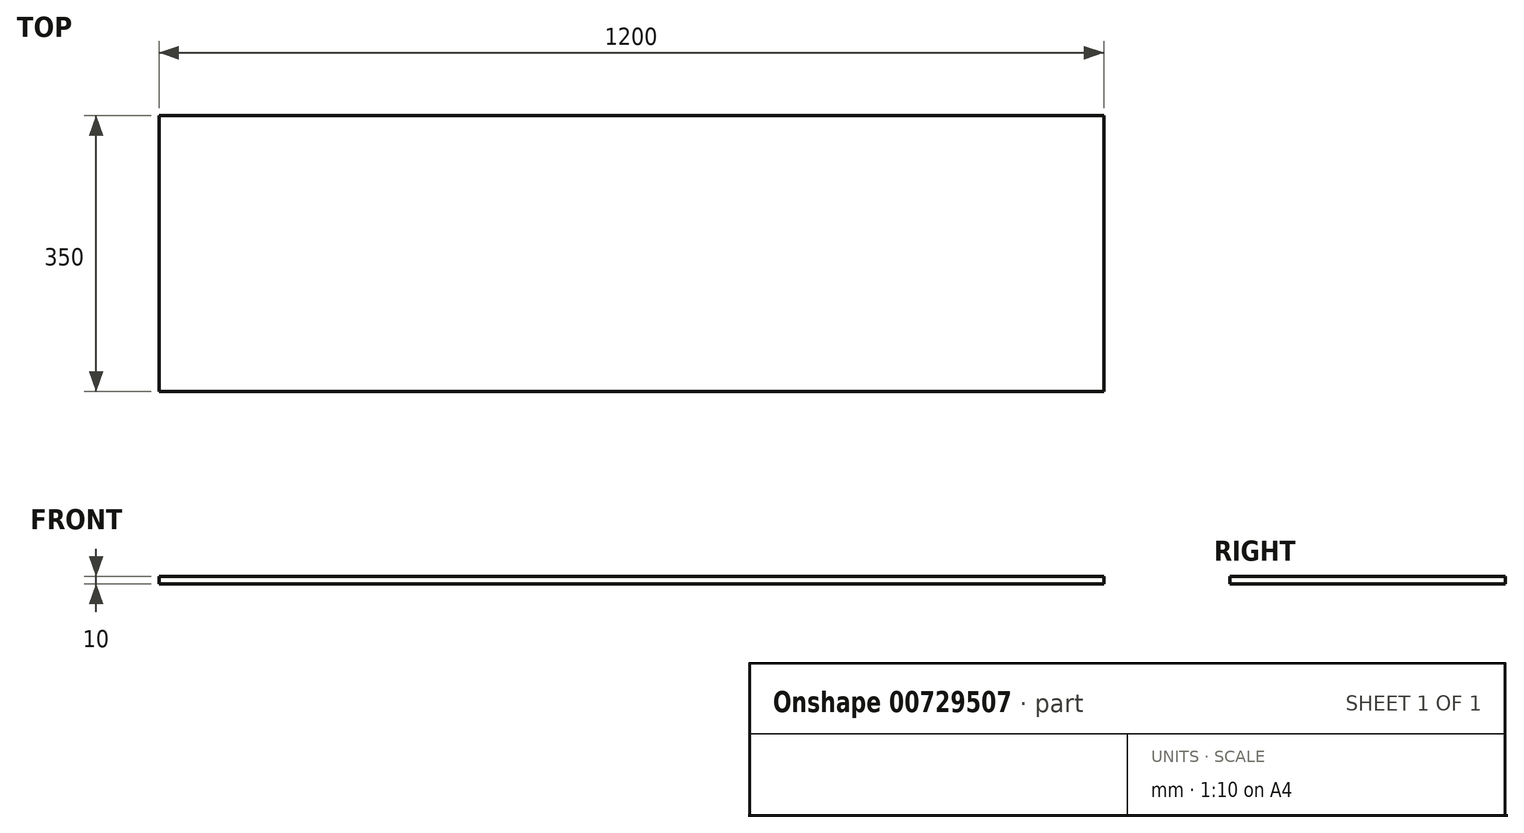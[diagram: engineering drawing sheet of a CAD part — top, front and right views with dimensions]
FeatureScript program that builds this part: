
annotation { "Feature Type Name" : "Feature", "Feature Type Description" : "" }
export const myFeature = defineFeature(function(context is Context, id is Id, definition is map)
    precondition{}
    {
        {
            var Q0;
            Q0=qCreatedBy(makeId("Top.planeOp"),FACE);
            var sketch = newSketch(context, id + "F0", { "sketchPlane" : qUnion([Q0])});
            skLineSegment(sketch, "E0.bottom", {"start": v(-584.07, 169.77) * mm, "end": v(615.93, 169.77) * mm});
            skLineSegment(sketch, "E0.top", {"start": v(-584.07, -180.23) * mm, "end": v(615.93, -180.23) * mm});
            skLineSegment(sketch, "E0.left", {"start": v(-584.07, 169.77) * mm, "end": v(-584.07, -180.23) * mm});
            skLineSegment(sketch, "E0.right", {"start": v(615.93, 169.77) * mm, "end": v(615.93, -180.23) * mm});
            skSolve(sketch);
        }
        {
            var Q0;
            Q0=makeQuery(id+"F0.imprint","IMPRINT",FACE,{"disambiguationData":[TD([[makeQuery(id+"F0.imprint","IMPRINT",EDGE,{"derivedFrom":sQuery(id+"F0.wireOp",EDGE,"E0.bottom")}),-1.0]])]});
            extrude(context, id + "F1", {"entities" : qUnion([Q0]), "depth" : 10 * mm, "offsetDistance" : 25 * mm});
        }
    });
